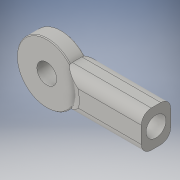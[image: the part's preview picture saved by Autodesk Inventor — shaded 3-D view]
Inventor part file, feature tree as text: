
AUTODESK INVENTOR PART (.ipt)
format: ipt  version: 2016 (Build 200138000, 138)  size: 198,144 bytes
history: native  units: in
note: dims shown in document units (in); Inventor stores cm internally (conversion verified against a paired STEP export)
features: extrude x6, sketch x5, fillet x2
ambient origin geometry x8: Origin, YZ Plane, XZ Plane, XY Plane, X Axis, Y Axis, Z Axis, Center Point
bodies: Solid1 (feature_tree)
feature tree (13):
  sketch  "Sketch1"  dims[d1=0.46in d9=0.37in d10=0.0in]
  extrude  "Extrusion3"  Depth=0.37in TaperAngle=0.0deg
  extrude  "Extrusion4"  Depth=0.9in
  extrude  "Extrusion6"  Depth=0.37in TaperAngle=0.0deg
  extrude  "Extrusion7"  Depth=0.092in TaperAngle=0.0deg
  extrude  "Extrusion8"  Depth=0.01in
  extrude  "Extrusion9"  Depth=0.01in TaperAngle=0.0deg
  fillet  "Fillet4"  Radius=0.25in
  fillet  "Fillet5"  Radius=0.7in
  sketch  "Sketch5"  dims[d11=0.76in d12=0.9in]
  sketch  "Sketch6"  dims[d13=180.0deg d14=0.37in d15=0.0in]
  sketch  "Sketch7"  dims[d18=90.0deg d19=0.092in d20=0.0in]
  sketch  "Sketch8"  dims[d21=0.092in d22=0.0in d23=0.25in d24=0.7in d25=0.0in d27=0.25in d28=0.7in d29=0.0in d32=0.125in d33=0.01in]
